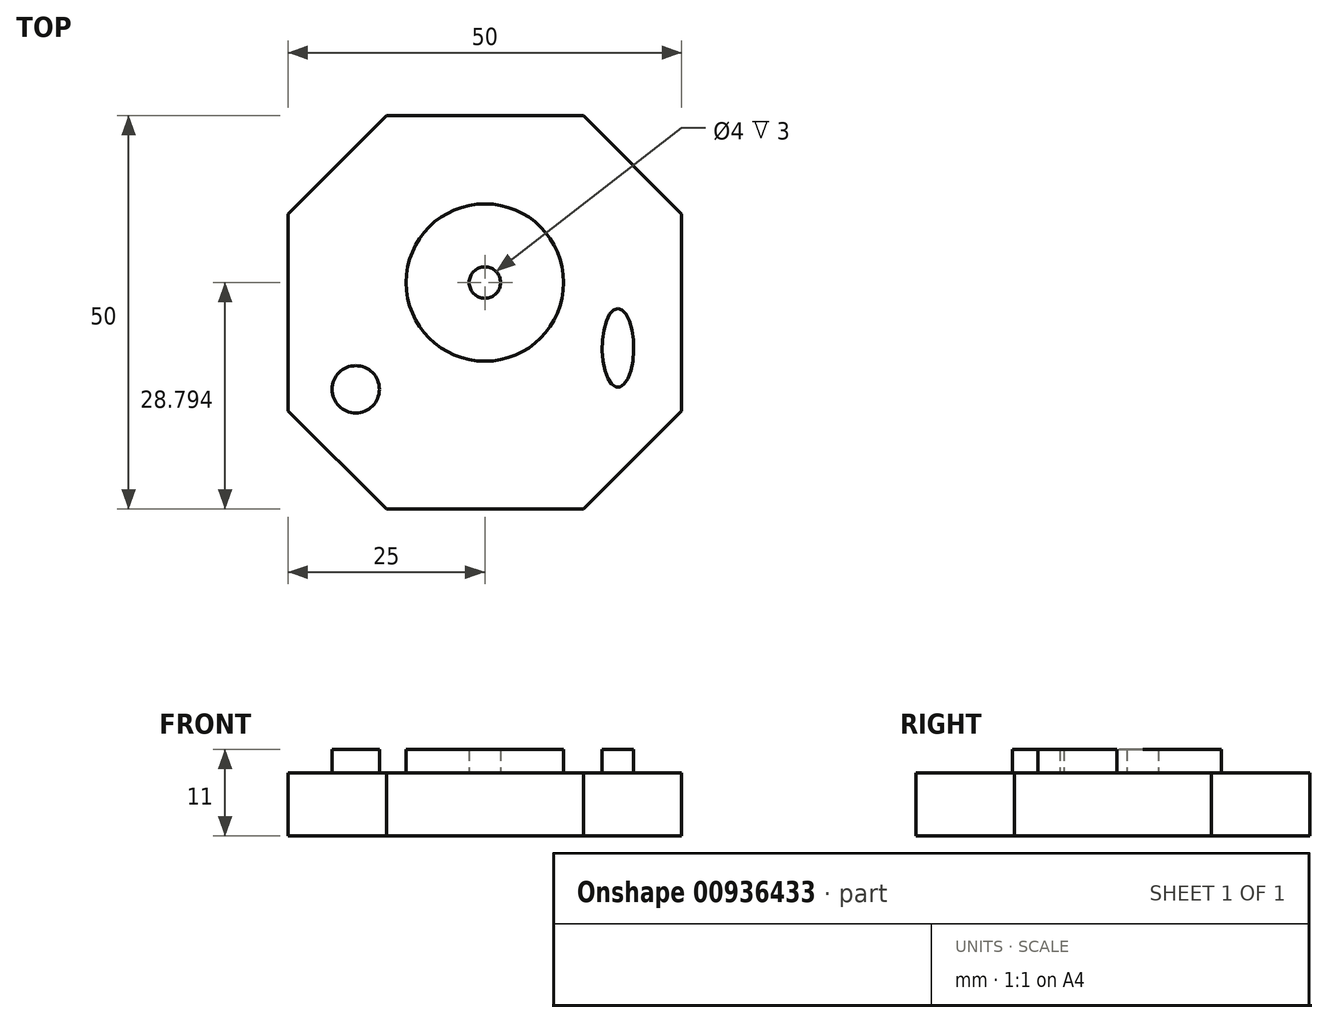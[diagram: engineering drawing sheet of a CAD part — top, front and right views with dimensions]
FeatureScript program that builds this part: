
annotation { "Feature Type Name" : "Feature", "Feature Type Description" : "" }
export const myFeature = defineFeature(function(context is Context, id is Id, definition is map)
    precondition{}
    {
        {
            var Q0;
            Q0=qCreatedBy(makeId("Top.planeOp"),FACE);
            var sketch = newSketch(context, id + "F0", { "sketchPlane" : qUnion([Q0])});
            skLineSegment(sketch, "E0.bottom", {"start": v(12.5, -25) * mm, "end": v(-12.5, -25) * mm});
            skLineSegment(sketch, "E0.top", {"start": v(12.5, 25) * mm, "end": v(-12.5, 25) * mm});
            skPoint(sketch, "E0.middle", {"position": v(0, 0) * mm});
            skLineSegment(sketch, "E1.left", {"start": v(25, -12.5) * mm, "end": v(25, 12.5) * mm});
            skLineSegment(sketch, "E1.right", {"start": v(-25, -12.5) * mm, "end": v(-25, 12.5) * mm});
            skLineSegment(sketch, "E2", {"start": v(12.5, 25) * mm, "end": v(25, 12.5) * mm});
            skLineSegment(sketch, "E3", {"start": v(-25, 12.5) * mm, "end": v(-12.5, 25) * mm});
            skLineSegment(sketch, "E4", {"start": v(-25, -12.5) * mm, "end": v(-12.5, -25) * mm});
            skLineSegment(sketch, "E5", {"start": v(12.5, -25) * mm, "end": v(25, -12.5) * mm});
            skSolve(sketch);
        }
        {
            var Q0;
            Q0=makeQuery(id+"F0.imprint","IMPRINT",FACE,{"disambiguationData":[TD([[makeQuery(id+"F0.imprint","IMPRINT",EDGE,{"derivedFrom":sQuery(id+"F0.wireOp",EDGE,"E0.bottom")}),-1.0]])]});
            extrude(context, id + "F1", {"entities" : qUnion([Q0]), "depth" : 8 * mm, "offsetDistance" : 25 * mm});
        }
        {
            var Q0;
            Q0=makeQuery(id+"F1.opExtrude","CAP_FACE",FACE,{"disambiguationData":[OSD([sQuery(id+"F0.wireOp",EDGE,"E0.bottom"),sQuery(id+"F0.wireOp",EDGE,"E0.top"),sQuery(id+"F0.wireOp",EDGE,"E1.left"),sQuery(id+"F0.wireOp",EDGE,"E1.right"),sQuery(id+"F0.wireOp",EDGE,"E2"),sQuery(id+"F0.wireOp",EDGE,"E3"),sQuery(id+"F0.wireOp",EDGE,"E4"),sQuery(id+"F0.wireOp",EDGE,"E5")])],"isStart":false});
            var sketch = newSketch(context, id + "F2", { "sketchPlane" : qUnion([Q0])});
            skCircle(sketch, "E6", {"center": v(0, 3.8) * mm, "radius": 10 * mm});
            skCircle(sketch, "E7", {"center": v(0, 3.8) * mm, "radius": 2 * mm});
            skEllipse(sketch, "E8", {"center": v(16.9, -4.5) * mm, "majorRadius": 5 * mm, "minorRadius": 2 * mm, "majorAxis": v(0, 1)});
            skCircle(sketch, "E9", {"center": v(-16.4, -9.77) * mm, "radius": 3 * mm});
            skSolve(sketch);
        }
        {
            var Q0;
            Q0 = qSketchRegion(id + "F2", true);
            extrude(context, id + "F3", {"entities" : qUnion([Q0]), "operationType" : NewBodyOperationType.ADD, "depth" : 3 * mm, "offsetDistance" : 25 * mm});
        }
    });
